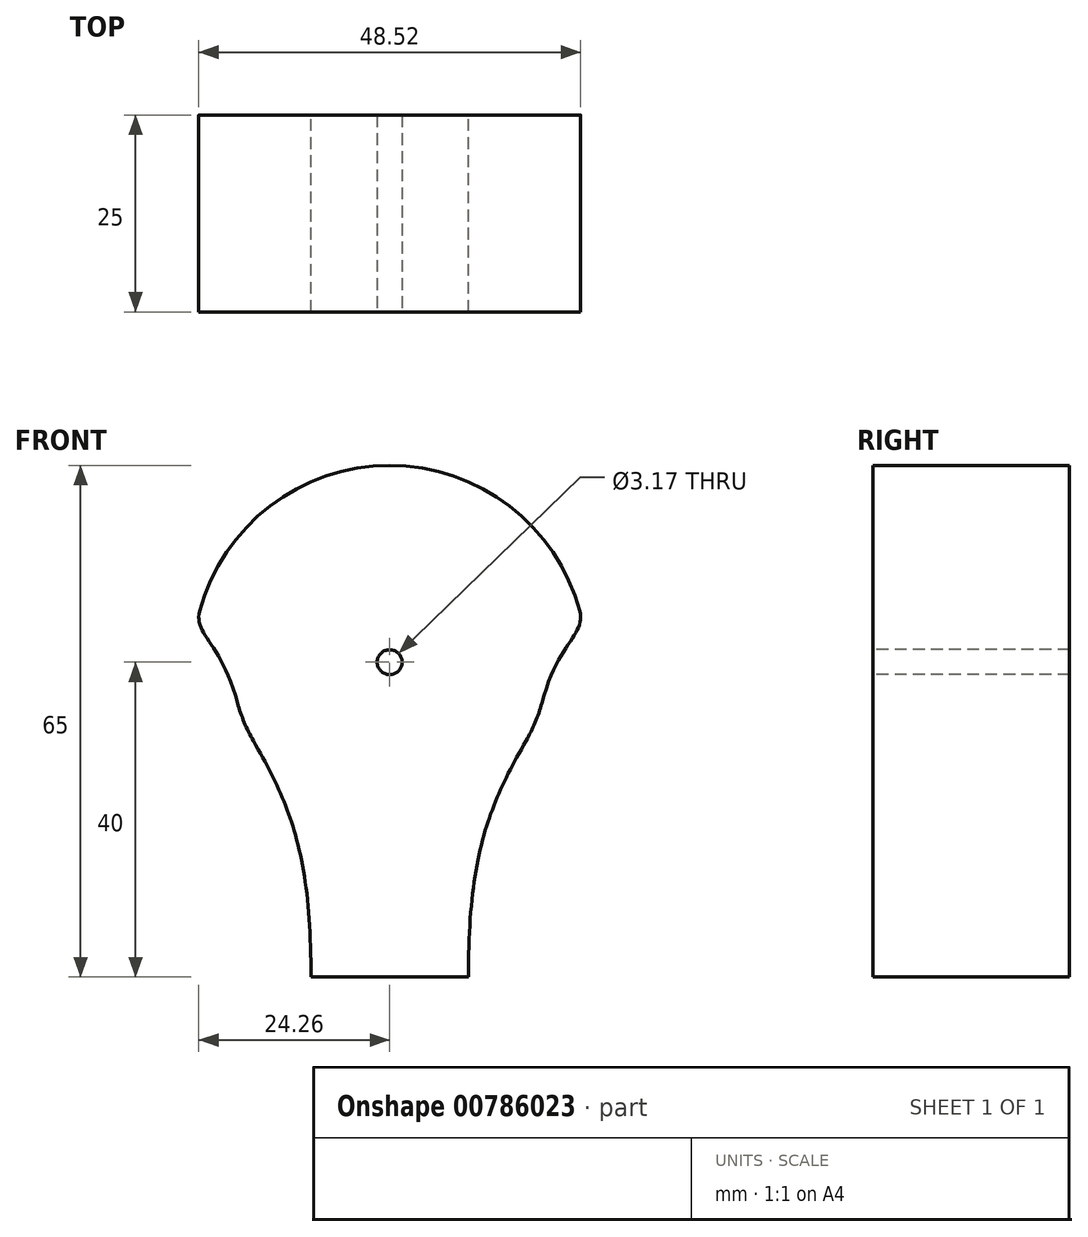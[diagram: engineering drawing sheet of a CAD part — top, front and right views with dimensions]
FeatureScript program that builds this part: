
annotation { "Feature Type Name" : "Feature", "Feature Type Description" : "" }
export const myFeature = defineFeature(function(context is Context, id is Id, definition is map)
    precondition{}
    {
        {
            var Q0;
            Q0=qCreatedBy(makeId("Front.planeOp"),FACE);
            var sketch = newSketch(context, id + "F0", { "sketchPlane" : qUnion([Q0])});
            skLineSegment(sketch, "E0.bottom", {"start": v(10, 0) * mm, "end": v(-10, 0) * mm, "construction": true});
            skLineSegment(sketch, "E0.top", {"start": v(10, -40) * mm, "end": v(-10, -40) * mm});
            skLineSegment(sketch, "E0.left", {"start": v(10, 0) * mm, "end": v(10, -40) * mm, "construction": true});
            skLineSegment(sketch, "E0.right", {"start": v(-10, 0) * mm, "end": v(-10, -40) * mm, "construction": true});
            skPoint(sketch, "E0.middle", {"position": v(0, -20) * mm});
            skCircle(sketch, "E1", {"center": v(0, 0) * mm, "radius": 20 * mm});
            skCircle(sketch, "E2", {"center": v(0, 0) * mm, "radius": 25 * mm});
            skLineSegment(sketch, "E3", {"start": v(0, 0) * mm, "end": v(24.15, 6.47) * mm});
            skLineSegment(sketch, "E4", {"start": v(0, 0) * mm, "end": v(19.32, -5.18) * mm});
            skLineSegment(sketch, "E5", {"start": v(0, 0) * mm, "end": v(17.32, -10) * mm});
            skLineSegment(sketch, "E6", {"start": v(0, 0) * mm, "end": v(21.65, 12.5) * mm});
            skFitSpline(sketch, "E7", {"points": [v(19.32, -5.18) * mm, v(24.15, 6.47) * mm], "startDerivative": vector(6.21, 23.18) * mm, "endDerivative": vector(-2.33, 8.7) * mm});
            skLineSegment(sketch, "E8", {"start": v(24.15, 6.47) * mm, "end": v(24.92, 3.57) * mm});
            skLineSegment(sketch, "E9", {"start": v(19.32, -5.18) * mm, "end": v(21.39, 2.55) * mm});
            skFitSpline(sketch, "E10", {"points": [v(17.32, -10) * mm, v(10, -40) * mm], "startDerivative": vector(-15, -25.98) * mm, "endDerivative": vector(0, -45) * mm});
            skLineSegment(sketch, "E11", {"start": v(17.32, -10) * mm, "end": v(12.32, -18.66) * mm});
            skLineSegment(sketch, "E12", {"start": v(0, -40) * mm, "end": v(0, 25) * mm, "construction": true});
            skFitSpline(sketch, "E13.MirrorCS", {"points": [v(-19.32, -5.18) * mm, v(-24.15, 6.47) * mm], "startDerivative": vector(-6.21, 23.18) * mm, "endDerivative": vector(2.33, 8.7) * mm});
            skFitSpline(sketch, "E14.MirrorCS", {"points": [v(-17.32, -10) * mm, v(-10, -40) * mm], "startDerivative": vector(15, -25.98) * mm, "endDerivative": vector(0, -45) * mm});
            skLineSegment(sketch, "E15.MirrorCS", {"start": v(0, 0) * mm, "end": v(-21.65, 12.5) * mm});
            skSolve(sketch);
        }
        {
            var Q0;
            {var subQ0=sQuery(id+"F0.wireOp",EDGE,"E6");var subQ1=sQuery(id+"F0.wireOp",EDGE,"E1");var subQ2=makeQuery(id+"F0.imprint","INTERSECT",VERTEX,{"derivedFrom":[subQ1,subQ0]});Q0=makeQuery(id+"F0.imprint","IMPRINT",FACE,{"disambiguationData":[TD([[makeQuery(id+"F0.imprint","IMPRINT",EDGE,{"disambiguationData":[TD([[subQ2,-1.0]])],"derivedFrom":subQ1}),1.0]])]});}
            var Q1;
            {var subQ0=sQuery(id+"F0.wireOp",EDGE,"E6");var subQ1=sQuery(id+"F0.wireOp",EDGE,"E1");var subQ2=makeQuery(id+"F0.imprint","INTERSECT",VERTEX,{"derivedFrom":[subQ1,subQ0]});Q1=makeQuery(id+"F0.imprint","IMPRINT",FACE,{"disambiguationData":[TD([[makeQuery(id+"F0.imprint","IMPRINT",EDGE,{"disambiguationData":[TD([[subQ2,-1.0]])],"derivedFrom":subQ1}),-1.0]])]});}
            var Q2;
            {var subQ0=sQuery(id+"F0.wireOp",EDGE,"E6");var subQ1=sQuery(id+"F0.wireOp",EDGE,"E1");var subQ2=makeQuery(id+"F0.imprint","INTERSECT",VERTEX,{"derivedFrom":[subQ1,subQ0]});Q2=makeQuery(id+"F0.imprint","IMPRINT",FACE,{"disambiguationData":[TD([[makeQuery(id+"F0.imprint","IMPRINT",EDGE,{"disambiguationData":[TD([[subQ2,1.0]])],"derivedFrom":subQ1}),-1.0]])]});}
            var Q3;
            {var subQ0=sQuery(id+"F0.wireOp",EDGE,"E6");var subQ1=sQuery(id+"F0.wireOp",EDGE,"E1");var subQ2=makeQuery(id+"F0.imprint","INTERSECT",VERTEX,{"derivedFrom":[subQ1,subQ0]});Q3=makeQuery(id+"F0.imprint","IMPRINT",FACE,{"disambiguationData":[TD([[makeQuery(id+"F0.imprint","IMPRINT",EDGE,{"disambiguationData":[TD([[subQ2,1.0]])],"derivedFrom":subQ1}),1.0]])]});}
            var Q4;
            {var subQ0=sQuery(id+"F0.wireOp",EDGE,"E4");Q4=makeQuery(id+"F0.imprint","IMPRINT",FACE,{"disambiguationData":[TD([[makeQuery(id+"F0.imprint","IMPRINT",EDGE,{"derivedFrom":subQ0}),1.0]])]});}
            var Q5;
            {var subQ0=sQuery(id+"F0.wireOp",EDGE,"E7");Q5=makeQuery(id+"F0.imprint","IMPRINT",FACE,{"disambiguationData":[TD([[makeQuery(id+"F0.imprint","IMPRINT",EDGE,{"derivedFrom":subQ0}),1.0]])]});}
            var Q6;
            {var subQ0=sQuery(id+"F0.wireOp",EDGE,"E4");Q6=makeQuery(id+"F0.imprint","IMPRINT",FACE,{"disambiguationData":[TD([[makeQuery(id+"F0.imprint","IMPRINT",EDGE,{"derivedFrom":subQ0}),-1.0]])]});}
            var Q7;
            {var subQ0=sQuery(id+"F0.wireOp",EDGE,"E5");Q7=makeQuery(id+"F0.imprint","IMPRINT",FACE,{"disambiguationData":[TD([[makeQuery(id+"F0.imprint","IMPRINT",EDGE,{"derivedFrom":subQ0}),-1.0]])]});}
            var Q8;
            {var subQ0=sQuery(id+"F0.wireOp",EDGE,"E0.top");Q8=makeQuery(id+"F0.imprint","IMPRINT",FACE,{"disambiguationData":[TD([[makeQuery(id+"F0.imprint","IMPRINT",EDGE,{"derivedFrom":subQ0}),-1.0]])]});}
            var Q9;
            {var subQ3=sQuery(id+"F0.wireOp",EDGE,"E14.MirrorCS");var subQ5=sQuery(id+"F0.wireOp",EDGE,"E2");var subQ6=makeQuery(id+"F0.imprint","INTERSECT",VERTEX,{"derivedFrom":[subQ5,subQ3]});Q9=makeQuery(id+"F0.imprint","IMPRINT",FACE,{"disambiguationData":[TD([[makeQuery(id+"F0.imprint","IMPRINT",EDGE,{"disambiguationData":[TD([[subQ6,-1.0]])],"derivedFrom":subQ5}),1.0]])]});}
            var Q10;
            {var subQ0=sQuery(id+"F0.wireOp",EDGE,"E13.MirrorCS");Q10=makeQuery(id+"F0.imprint","IMPRINT",FACE,{"disambiguationData":[TD([[makeQuery(id+"F0.imprint","IMPRINT",EDGE,{"derivedFrom":subQ0}),-1.0]])]});}
            extrude(context, id + "F1", {"entities" : qUnion([Q0, Q1, Q2, Q3, Q4, Q5, Q6, Q7, Q8, Q9, Q10]), "depth" : 25 * mm, "offsetDistance" : 25 * mm});
        }
        {
            var Q0;
            Q0=makeQuery(id+"F1.opExtrude","CAP_FACE",FACE,{"disambiguationData":[OSD([sQuery(id+"F0.wireOp",EDGE,"E0.top"),sQuery(id+"F0.wireOp",EDGE,"E1"),sQuery(id+"F0.wireOp",EDGE,"E2"),sQuery(id+"F0.wireOp",EDGE,"E7"),sQuery(id+"F0.wireOp",EDGE,"E10"),sQuery(id+"F0.wireOp",EDGE,"E13.MirrorCS"),sQuery(id+"F0.wireOp",EDGE,"E14.MirrorCS")])],"isStart":false});
            var sketch = newSketch(context, id + "F2", { "sketchPlane" : qUnion([Q0])});
            skCircle(sketch, "E16", {"center": v(0, 0) * mm, "radius": 1.59 * mm});
            skSolve(sketch);
        }
        {
            var Q0;
            Q0=qSketchRegion(id+"F2",true);
            extrude(context, id + "F3", {"entities" : qUnion([Q0]), "operationType" : NewBodyOperationType.REMOVE, "oppositeDirection" : true, "depth" : 25 * mm, "offsetDistance" : 25 * mm});
        }
    });
